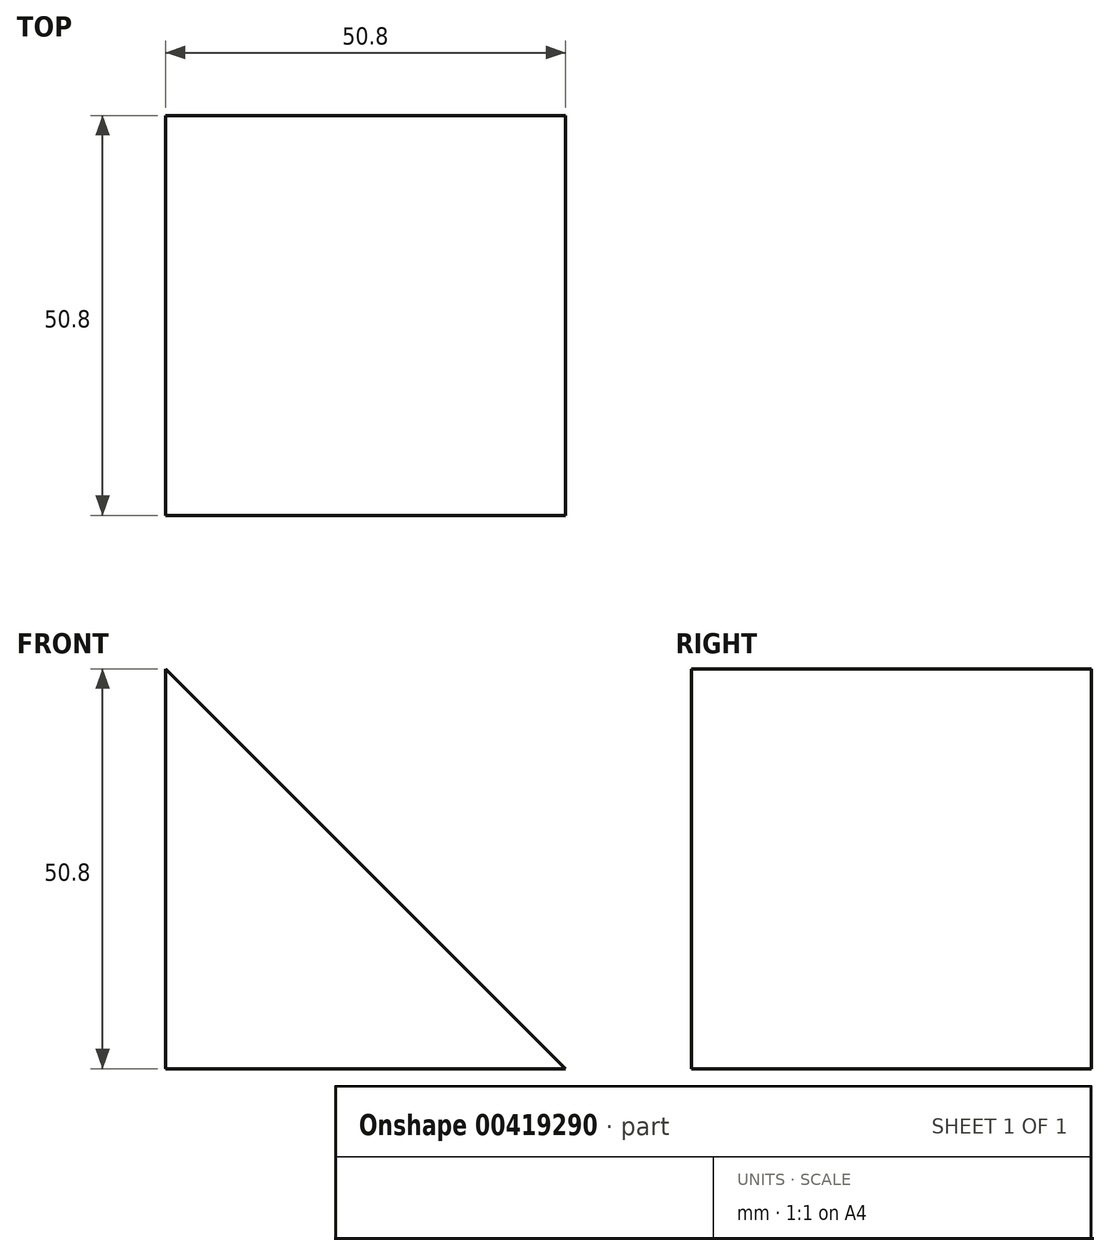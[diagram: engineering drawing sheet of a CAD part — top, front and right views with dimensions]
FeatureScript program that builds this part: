
annotation { "Feature Type Name" : "Feature", "Feature Type Description" : "" }
export const myFeature = defineFeature(function(context is Context, id is Id, definition is map)
    precondition{}
    {
        {
            var Q0;
            Q0=qCreatedBy(makeId("Front.planeOp"),FACE);
            var sketch = newSketch(context, id + "F0", { "sketchPlane" : qUnion([Q0])});
            skLineSegment(sketch, "E0", {"start": v(-50.8, 42.2) * mm, "end": v(-50.8, -8.6) * mm});
            skLineSegment(sketch, "E1", {"start": v(-50.8, -8.6) * mm, "end": v(0, -8.6) * mm});
            skLineSegment(sketch, "E2", {"start": v(0, -8.6) * mm, "end": v(-50.8, 42.2) * mm});
            skSolve(sketch);
        }
        {
            var Q0;
            Q0=makeQuery(id+"F0.imprint","IMPRINT",FACE,{"disambiguationData":[TD([[makeQuery(id+"F0.imprint","IMPRINT",EDGE,{"derivedFrom":sQuery(id+"F0.wireOp",EDGE,"E0")}),1.0]])]});
            extrude(context, id + "F1", {"entities" : qUnion([Q0]), "oppositeDirection" : true, "depth" : 50.8 * mm});
        }
    });
